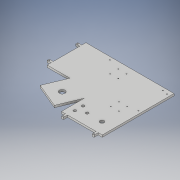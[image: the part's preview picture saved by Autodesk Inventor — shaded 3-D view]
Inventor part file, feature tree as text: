
AUTODESK INVENTOR PART (.ipt)
format: ipt  version: 2018 (Build 220112000, 112)  size: 264,192 bytes
history: native  units: in
note: dims shown in document units (in); Inventor stores cm internally (conversion verified against a paired STEP export)
features: extrude x10, sketch x10, projected_geometry x3
ambient origin geometry x8: Origin, YZ Plane, XZ Plane, XY Plane, X Axis, Y Axis, Z Axis, Center Point
bodies: Solid1 (feature_tree)
feature tree (23):
  extrude  "Extrusion1"  Depth=4.75in
  extrude  "Extrusion2"  Depth=6.0in
  extrude  "Extrusion3"  Depth=0.25in TaperAngle=0.0deg
  extrude  "Extrusion4"  Depth=2.8in TaperAngle=0.0deg
  extrude  "Extrusion5"  Depth=0.25in
  extrude  "Extrusion6"  Depth=0.125in
  extrude  "Extrusion7"  Depth=0.5in
  extrude  "Extrusion8"  Depth=0.5in
  extrude  "Extrusion9"  Depth=0.25in
  extrude  "Extrusion10"  Depth=0.5in
  sketch  "Sketch1"  dims[d0=8.0in d1=4.75in]
  sketch  "Sketch3"  dims[d2=5.0in d3=6.0in]
  projected_geometry  "Projected Loop1"
  sketch  "Sketch4"  dims[d4=0.25in d5=0.0in d6=2.8in d7=0.0in]
  projected_geometry  "Projected Loop2"
  sketch  "Sketch5"  dims[d8=2.8in d9=0.0in d10=2.8in d11=0.0in]
  projected_geometry  "Projected Loop3"
  sketch  "Sketch7"  dims[d13=0.5in d14=0.25in]
  sketch  "Sketch8"  dims[d15=0.11in d16=0.125in]
  sketch  "Sketch9"  dims[d17=0.5in d18=0.125in]
  sketch  "Sketch10"  dims[d19=0.5in d20=0.25in d21=0.11in d22=0.125in d23=0.125in d24=0.0in d25=0.5in]
  sketch  "Sketch11"  dims[d26=0.25in d27=0.0in d33=0.25in]
  sketch  "Sketch12"  dims[d34=0.5in d35=0.5in d36=0.11in d37=0.125in d38=0.125in d39=0.25in d40=0.5in d41=0.11in d42=0.125in d43=0.125in d44=0.0in d45=0.5in d46=0.25in d47=0.0in d48=0.11in d49=0.11in d50=0.11in d51=0.11in d52=1.0in d53=1.0in d54=1.0in d55=1.0in d56=1.0in d57=1.0in d58=0.75in d59=1.5in d60=0.11in d61=0.11in d62=0.11in d63=0.11in d64=1.0in d65=1.0in d66=1.0in d67=1.0in d68=1.0in d69=1.0in d70=0.25in d71=0.0in d72=0.12in d73=0.12in d74=0.5in d75=3.5in d76=0.365in d77=0.365in d78=0.12in d79=0.12in d80=0.365in d81=1.0in d82=0.5in d83=0.365in d84=0.25in d85=0.0in d86=0.335in d87=0.335in d88=0.335in d89=0.69in d90=0.9in d91=0.9in d92=1.4in d93=1.75in d94=0.75in d95=0.75in d96=0.25in d97=0.0in d98=0.5in d99=0.25in d100=0.0in]
